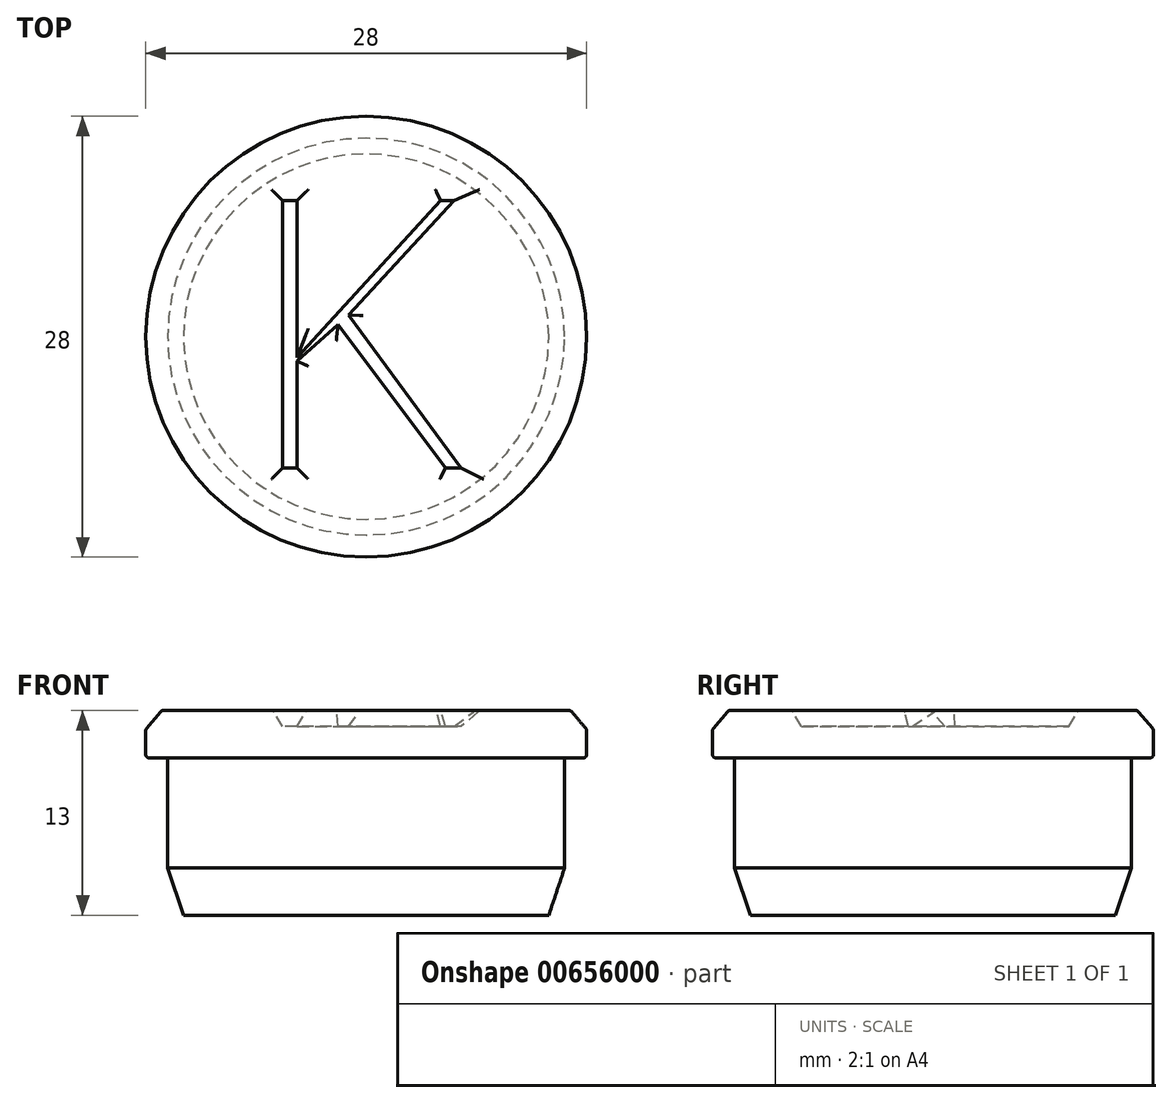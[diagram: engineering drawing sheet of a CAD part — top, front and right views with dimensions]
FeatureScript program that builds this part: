
annotation { "Feature Type Name" : "Feature", "Feature Type Description" : "" }
export const myFeature = defineFeature(function(context is Context, id is Id, definition is map)
    precondition{}
    {
        {
            var Q0;
            Q0=qCreatedBy(makeId("Top.planeOp"),FACE);
            var sketch = newSketch(context, id + "F0", { "sketchPlane" : qUnion([Q0])});
            skCircle(sketch, "E0", {"center": v(0, 0) * mm, "radius": 12.6 * mm});
            skCircle(sketch, "E1", {"center": v(0, 0) * mm, "radius": 14 * mm});
            skText(sketch, "E2", { "text": "K", "fontName": "OpenSans-Regular.ttf"});
            const initialGuessF0  = {"E2": [-0.0084, -0.00894, 1, 0, 0.01833]};
            skSetInitialGuess(sketch, initialGuessF0);
            skSolve(sketch);
        }
        {
            var Q0;
            Q0=makeQuery(id+"F0.imprint","IMPRINT",FACE,{"disambiguationData":[TD([[makeQuery(id+"F0.imprint","IMPRINT",EDGE,{"derivedFrom":sQuery(id+"F0.wireOp",EDGE,"E2.sketch_text.stroke-11")}),1.0]])]});
            var Q1;
            Q1=makeQuery(id+"F0.imprint","IMPRINT",FACE,{"disambiguationData":[TD([[makeQuery(id+"F0.imprint","IMPRINT",EDGE,{"derivedFrom":sQuery(id+"F0.wireOp",EDGE,"E2.sketch_text.stroke-0")}),-1.0]])]});
            var Q2;
            Q2=makeQuery(id+"F0.imprint","IMPRINT",FACE,{"disambiguationData":[TD([[makeQuery(id+"F0.imprint","IMPRINT",EDGE,{"derivedFrom":sQuery(id+"F0.wireOp",EDGE,"E0")}),1.0]])]});
            extrude(context, id + "F1", {"entities" : qUnion([Q0, Q1, Q2]), "oppositeDirection" : true, "depth" : 13 * mm, "offsetDistance" : 25 * mm});
        }
        {
            var Q0;
            Q0=makeQuery(id+"F0.imprint","IMPRINT",FACE,{"disambiguationData":[TD([[makeQuery(id+"F0.imprint","IMPRINT",EDGE,{"derivedFrom":sQuery(id+"F0.wireOp",EDGE,"E0")}),-1.0]])]});
            extrude(context, id + "F2", {"entities" : qUnion([Q0]), "operationType" : NewBodyOperationType.ADD, "oppositeDirection" : true, "depth" : 3 * mm, "offsetDistance" : 25 * mm});
        }
        {
            var Q0;
            Q0=makeQuery(id+"F1.opExtrude","CAP_EDGE",EDGE,{"disambiguationData":[OSD([sQuery(id+"F0.wireOp",EDGE,"E0")])],"isStart":false});
            chamfer(context, id + "F3", {"entities" : qUnion([Q0]), "chamferType" : ChamferType.TWO_OFFSETS, "width1" : 1 * mm, "oppositeDirection" : true, "width2" : 3 * mm, "tangentPropagation" : true});
        }
        {
            var Q0;
            Q0=makeQuery(id+"F2.opExtrude","CAP_EDGE",EDGE,{"disambiguationData":[OSD([sQuery(id+"F0.wireOp",EDGE,"E1")])],"isStart":true});
            chamfer(context, id + "F4", {"entities" : qUnion([Q0]), "chamferType" : ChamferType.TWO_OFFSETS, "width1" : 1.2 * mm, "oppositeDirection" : true, "width2" : 1 * mm, "tangentPropagation" : true});
        }
        {
            var Q0;
            Q0=makeQuery(id+"F0.imprint","IMPRINT",FACE,{"disambiguationData":[TD([[makeQuery(id+"F0.imprint","IMPRINT",EDGE,{"derivedFrom":sQuery(id+"F0.wireOp",EDGE,"E2.sketch_text.stroke-0")}),-1.0]])]});
            extrude(context, id + "F5", {"entities" : qUnion([Q0]), "operationType" : NewBodyOperationType.REMOVE, "oppositeDirection" : true, "depth" : 1 * mm, "offsetDistance" : 25 * mm});
        }
        {
            var Q0;
            Q0=makeQuery(id+"F5.boolean.opBoolean","COPY",FACE,{"derivedFrom":makeQuery(id+"F5.opExtrude","CAP_FACE",FACE,{"disambiguationData":[OSD([sQuery(id+"F0.wireOp",EDGE,"E2.sketch_text.stroke-0"),sQuery(id+"F0.wireOp",EDGE,"E2.sketch_text.stroke-1"),sQuery(id+"F0.wireOp",EDGE,"E2.sketch_text.stroke-2"),sQuery(id+"F0.wireOp",EDGE,"E2.sketch_text.stroke-3"),sQuery(id+"F0.wireOp",EDGE,"E2.sketch_text.stroke-4"),sQuery(id+"F0.wireOp",EDGE,"E2.sketch_text.stroke-5"),sQuery(id+"F0.wireOp",EDGE,"E2.sketch_text.stroke-6"),sQuery(id+"F0.wireOp",EDGE,"E2.sketch_text.stroke-7"),sQuery(id+"F0.wireOp",EDGE,"E2.sketch_text.stroke-8"),sQuery(id+"F0.wireOp",EDGE,"E2.sketch_text.stroke-9"),sQuery(id+"F0.wireOp",EDGE,"E2.sketch_text.stroke-10"),sQuery(id+"F0.wireOp",EDGE,"E2.sketch_text.stroke-11"),sQuery(id+"F0.wireOp",EDGE,"E2.sketch_text.stroke-12"),sQuery(id+"F0.wireOp",EDGE,"E2.sketch_text.stroke-13"),sQuery(id+"F0.wireOp",EDGE,"E2.sketch_text.stroke-14"),sQuery(id+"F0.wireOp",EDGE,"E2.sketch_text.stroke-15"),sQuery(id+"F0.wireOp",EDGE,"E2.sketch_text.stroke-16"),sQuery(id+"F0.wireOp",EDGE,"E2.sketch_text.stroke-17")])],"isStart":false})});
            chamfer(context, id + "F6", {"entities" : qUnion([Q0]), "chamferType" : ChamferType.TWO_OFFSETS, "width1" : 1 * mm, "oppositeDirection" : false, "width2" : 0.6 * mm, "tangentPropagation" : true});
        }
        {
            var Q0;
            {var subQ0=sQuery(id+"F0.wireOp",EDGE,"E1");var subQ1=sQuery(id+"F0.wireOp",EDGE,"E0");Q0=makeQuery(id+"F5.boolean.opBoolean","SPLIT",FACE,{"disambiguationData":[TD([makeQuery(id+"F4.opChamfer","BLEND_FACE",FACE,{"disambiguationData":[OSD([subQ0])]})])],"derivedFrom":makeQuery(id+"F2.boolean.opBoolean","MERGE",FACE,{"derivedFrom":[makeQuery(id+"F1.opExtrude","CAP_FACE",FACE,{"disambiguationData":[OSD([subQ1])],"isStart":true}),makeQuery(id+"F2.opExtrude","CAP_FACE",FACE,{"disambiguationData":[OSD([subQ1,subQ0])],"isStart":true})]})});}
            var Q1;
            {var subQ0=sQuery(id+"F0.wireOp",EDGE,"E1");Q1=makeQuery(id+"F4.opChamfer","BLEND_EDGE",EDGE,{"blendedFrom":[makeQuery(id+"F2.opExtrude","CAP_EDGE",EDGE,{"disambiguationData":[OSD([subQ0])],"isStart":true}),makeQuery(id+"F2.opExtrude","SWEPT_FACE",FACE,{"disambiguationData":[OSD([subQ0])]})],"blendedInto":[makeQuery(id+"F2.opExtrude","SWEPT_FACE",FACE,{"disambiguationData":[OSD([subQ0])]})]});}
            var Q2;
            Q2=makeQuery(id+"F2.opExtrude","CAP_EDGE",EDGE,{"disambiguationData":[OSD([sQuery(id+"F0.wireOp",EDGE,"E1")])],"isStart":false});
            fillet(context, id + "F7", {"entities" : qUnion([Q0, Q1, Q2]), "radius" : 0.2 * mm, "tangentPropagation" : true, "allowEdgeOverflow" : false});
        }
    });
